# Revit family: Urinal-Wall_Mount-KOHLER-BARDON-K-4960T_1
name_source: partatom
category: Plumbing Fixtures
revit_build: Autodesk Revit 2017 (Build: 20160225_1515(x64)
units: mm (PartAtom-declared; Revit-internal decimal feet)

## family parameters
Cut with Voids When Loaded = No
Host = Face
OmniClass Number = 23.31.21.00
OmniClass Title = Urinals
Part Type = Normal
Room Calculation Point = No
Round Connector Dimension = Use Diameter
Shared = No

## types (2) — shared parameters
ADA Compliant = No
Assembly Code = D2010200
CW Connection = Yes
Cold Water Inlet = Cold Water Inlet
Date Modified = 07/13/2021
Default Elevation = 0"
Finish = Kohler-Vitreous_China-0-White
Flow Rate = 0 GPM
Flush Rate- GPF = GPF
Flush Rate- LPF = LPF
HW Connection = No
Height = 26 3/8"
Hot Water Inlet = Hot Water Inlet
Length = 14 1/16"
Manufacturer = KOHLER Co.
Master Format 2014 = 22 41 13.16
Master Format 2014 Name = Residential Urinals
Material = Vitreous China
Pressure = 0.00 psi
Product Name = BARDON
URL = http://www.kohler.com.cn
Vent Connection = No
Waste Connection = Yes
Waste Water Outlet = Waste Water Outlet
WaterSense Certified = No
Width = 18 1/4"

## per-type parameters (varying)
| type | Cut Height | Description | Model | Rear Water Inlet | Type | Upper Water Inlet |
| Upper Water Inlet, 0-White | 0" | URINAL TOP INLET | K-4960T-ET-0 | No | 1 | Yes |
| Rear Water Inlet, 0-White | 1 1/4" | URINAL REAR INLET | K-4960T-ER-0 | Yes | 2 | No |

## geometry (parser evidence)
native form markers: Sweep x4
no freeform markers — native parametric forms only
